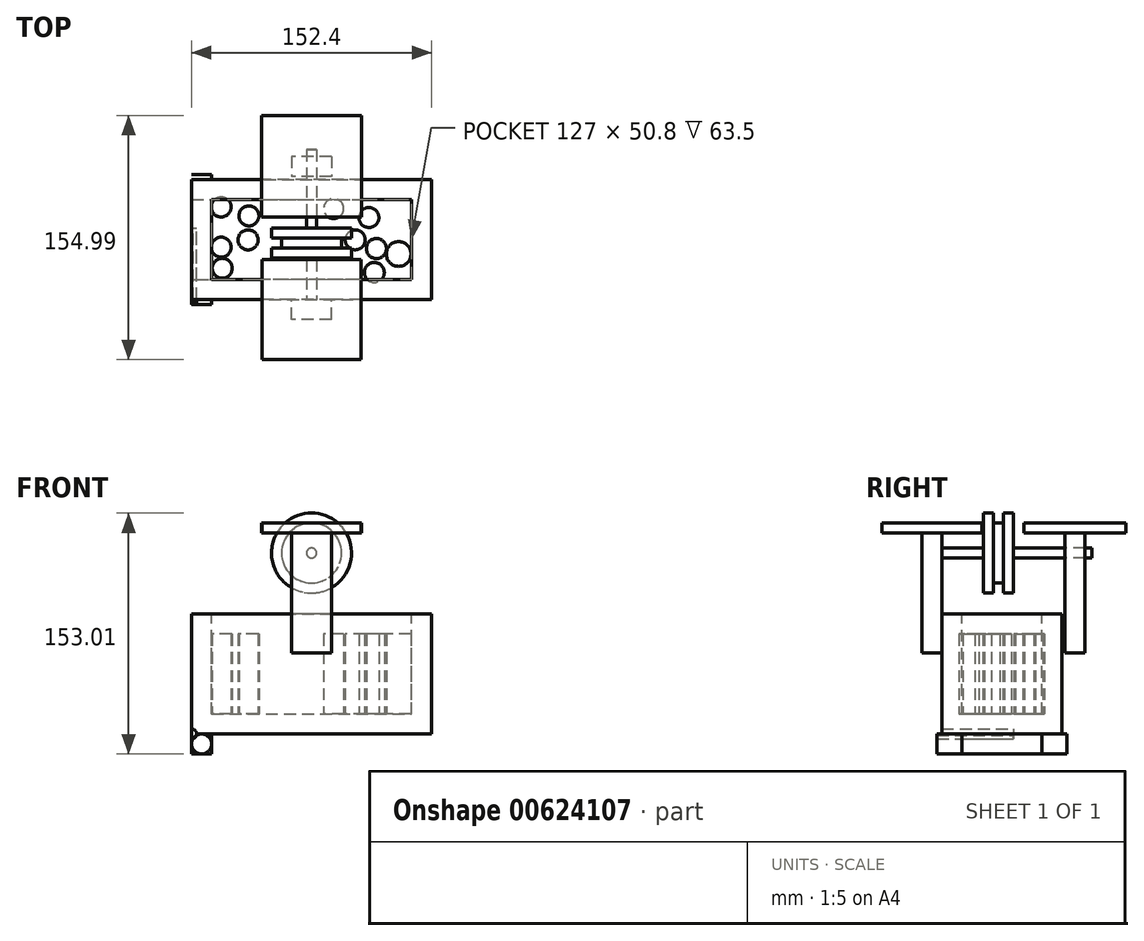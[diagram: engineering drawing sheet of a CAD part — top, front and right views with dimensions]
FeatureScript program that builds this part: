
annotation { "Feature Type Name" : "Feature", "Feature Type Description" : "" }
export const myFeature = defineFeature(function(context is Context, id is Id, definition is map)
    precondition{}
    {
        {
            var Q0;
            Q0=qCreatedBy(makeId("Front.planeOp"),FACE);
            var sketch = newSketch(context, id + "F0", { "sketchPlane" : qUnion([Q0])});
            skLineSegment(sketch, "E0", {"start": v(0, 0) * mm, "end": v(152.4, 0) * mm});
            skLineSegment(sketch, "E1", {"start": v(152.4, 0) * mm, "end": v(152.4, 76.2) * mm});
            skLineSegment(sketch, "E2", {"start": v(152.4, 76.2) * mm, "end": v(0, 76.2) * mm});
            skLineSegment(sketch, "E3", {"start": v(0, 76.2) * mm, "end": v(0, 0) * mm});
            skSolve(sketch);
        }
        {
            var Q0;
            Q0=makeQuery(id+"F0.imprint","IMPRINT",FACE,{"disambiguationData":[TD([[makeQuery(id+"F0.imprint","IMPRINT",EDGE,{"derivedFrom":sQuery(id+"F0.wireOp",EDGE,"E0")}),1.0]])]});
            extrude(context, id + "F1", {"entities" : qUnion([Q0]), "oppositeDirection" : true, "depth" : 76.2 * mm, "offsetDistance" : 25.4 * mm});
        }
        {
            var Q0;
            Q0=makeQuery(id+"F1.opExtrude","SWEPT_FACE",FACE,{"disambiguationData":[OSD([sQuery(id+"F0.wireOp",EDGE,"E2")])]});
            var sketch = newSketch(context, id + "F2", { "sketchPlane" : qUnion([Q0])});
            skLineSegment(sketch, "E4", {"start": v(12.7, 63.5) * mm, "end": v(12.7, 12.7) * mm});
            skLineSegment(sketch, "E5", {"start": v(12.7, 63.5) * mm, "end": v(139.7, 63.5) * mm});
            skLineSegment(sketch, "E6", {"start": v(139.7, 12.7) * mm, "end": v(139.7, 63.5) * mm});
            skLineSegment(sketch, "E7", {"start": v(139.7, 12.7) * mm, "end": v(12.7, 12.7) * mm});
            skSolve(sketch);
        }
        {
            var Q0;
            Q0=makeQuery(id+"F2.imprint","IMPRINT",FACE,{"disambiguationData":[TD([[makeQuery(id+"F2.imprint","IMPRINT",EDGE,{"derivedFrom":sQuery(id+"F2.wireOp",EDGE,"E4")}),1.0]])]});
            extrude(context, id + "F3", {"entities" : qUnion([Q0]), "operationType" : NewBodyOperationType.REMOVE, "oppositeDirection" : true, "depth" : 63.5 * mm, "offsetDistance" : 25.4 * mm});
        }
        {
            var Q0;
            Q0=makeQuery(id+"F1.opExtrude","CAP_FACE",FACE,{"disambiguationData":[OSD([sQuery(id+"F0.wireOp",EDGE,"E0"),sQuery(id+"F0.wireOp",EDGE,"E1"),sQuery(id+"F0.wireOp",EDGE,"E2"),sQuery(id+"F0.wireOp",EDGE,"E3")])],"isStart":true});
            var sketch = newSketch(context, id + "F4", { "sketchPlane" : qUnion([Q0])});
            skLineSegment(sketch, "E8", {"start": v(76.2, 0) * mm, "end": v(76.2, 51.42) * mm});
            skLineSegment(sketch, "E9", {"start": v(76.2, 51.42) * mm, "end": v(88.9, 51.42) * mm});
            skLineSegment(sketch, "E10", {"start": v(76.2, 51.42) * mm, "end": v(63.5, 51.42) * mm});
            skLineSegment(sketch, "E11", {"start": v(63.5, 51.42) * mm, "end": v(63.5, 64.12) * mm});
            skLineSegment(sketch, "E12", {"start": v(88.9, 51.42) * mm, "end": v(88.9, 64.12) * mm});
            skLineSegment(sketch, "E13", {"start": v(63.5, 64.12) * mm, "end": v(88.9, 64.12) * mm});
            skSolve(sketch);
        }
        {
            var Q0;
            Q0 = qSketchRegion(id + "F4", true);
            extrude(context, id + "F5", {"entities" : qUnion([Q0]), "depth" : 12.7 * mm, "offsetDistance" : 25.4 * mm});
        }
        {
            var Q0;
            Q0=makeQuery(id+"F5.opExtrude","SWEPT_FACE",FACE,{"disambiguationData":[OSD([sQuery(id+"F4.wireOp",EDGE,"E13")])]});
            var sketch = newSketch(context, id + "F6", { "sketchPlane" : qUnion([Q0])});
            skLineSegment(sketch, "E14", {"start": v(63.5, -12.7) * mm, "end": v(63.5, 0) * mm});
            skLineSegment(sketch, "E15", {"start": v(63.5, 0) * mm, "end": v(88.9, 0) * mm});
            skLineSegment(sketch, "E16", {"start": v(88.9, 0) * mm, "end": v(88.9, -12.7) * mm});
            skLineSegment(sketch, "E17", {"start": v(88.9, -12.7) * mm, "end": v(63.5, -12.7) * mm});
            skSolve(sketch);
        }
        {
            var Q0;
            Q0 = qSketchRegion(id + "F6", true);
            extrude(context, id + "F7", {"entities" : qUnion([Q0]), "depth" : 63.5 * mm, "offsetDistance" : 25.4 * mm});
        }
        {
            var Q0;
            Q0=qCreatedBy(makeId("Front.planeOp"),FACE);
            cPlane(context, id + "F8", {"entities" : qUnion([Q0]), "cplaneType" : CPlaneType.OFFSET, "offset" : 39.12 * mm, "oppositeDirection" : true, "width" : 152.4 * mm, "height" : 152.4 * mm});
        }
        {
            var Q0;
            Q0=makeQuery(id+"F5.opExtrude","SWEPT_BODY",BODY,{"disambiguationData":[OSD([sQuery(id+"F4.wireOp",EDGE,"E9"),sQuery(id+"F4.wireOp",EDGE,"E10"),sQuery(id+"F4.wireOp",EDGE,"E11"),sQuery(id+"F4.wireOp",EDGE,"E12"),sQuery(id+"F4.wireOp",EDGE,"E13")])]});
            var Q1;
            Q1=makeQuery(id+"F7.opExtrude","SWEPT_BODY",BODY,{"disambiguationData":[OSD([sQuery(id+"F6.wireOp",EDGE,"E14"),sQuery(id+"F6.wireOp",EDGE,"E15"),sQuery(id+"F6.wireOp",EDGE,"E16"),sQuery(id+"F6.wireOp",EDGE,"E17")])]});
            var Q2;
            Q2=qCreatedBy(id+"F8.planeOp",FACE);
            mirror(context, id + "F9", {"operationType" : NewBodyOperationType.ADD, "entities" : qUnion([Q0, Q1]), "mirrorPlane" : qUnion([Q2])});
        }
        {
            var Q0;
            Q0=makeQuery(id+"F9.boolean.opBoolean","MERGE",FACE,{"derivedFrom":[makeQuery(id+"F5.opExtrude","CAP_FACE",FACE,{"disambiguationData":[OSD([sQuery(id+"F4.wireOp",EDGE,"E9"),sQuery(id+"F4.wireOp",EDGE,"E10"),sQuery(id+"F4.wireOp",EDGE,"E11"),sQuery(id+"F4.wireOp",EDGE,"E12"),sQuery(id+"F4.wireOp",EDGE,"E13")])],"isStart":true}),makeQuery(id+"F7.opExtrude","SWEPT_FACE",FACE,{"disambiguationData":[OSD([sQuery(id+"F6.wireOp",EDGE,"E15")])]})]});
            var sketch = newSketch(context, id + "F10", { "sketchPlane" : qUnion([Q0])});
            skLineSegment(sketch, "E18", {"start": v(-76.2, 127.62) * mm, "end": v(-76.2, 114.92) * mm});
            skCircle(sketch, "E19", {"center": v(-76.2, 114.92) * mm, "radius": 3.18 * mm});
            skSolve(sketch);
        }
        {
            var Q0;
            Q0 = qSketchRegion(id + "F10", true);
            extrude(context, id + "F11", {"entities" : qUnion([Q0]), "depth" : 95.25 * mm, "offsetDistance" : 25.4 * mm});
        }
        {
            var Q0;
            Q0=makeQuery(id+"F7.opExtrude","CAP_FACE",FACE,{"disambiguationData":[OSD([sQuery(id+"F6.wireOp",EDGE,"E14"),sQuery(id+"F6.wireOp",EDGE,"E15"),sQuery(id+"F6.wireOp",EDGE,"E16"),sQuery(id+"F6.wireOp",EDGE,"E17")])],"isStart":false});
            var sketch = newSketch(context, id + "F12", { "sketchPlane" : qUnion([Q0])});
            skLineSegment(sketch, "E20.bottom", {"start": v(107.68, 25.4) * mm, "end": v(44.72, 25.4) * mm});
            skLineSegment(sketch, "E20.top", {"start": v(107.68, -38.1) * mm, "end": v(44.72, -38.1) * mm});
            skLineSegment(sketch, "E20.left", {"start": v(107.68, 25.4) * mm, "end": v(107.68, -38.1) * mm});
            skLineSegment(sketch, "E20.right", {"start": v(44.72, 25.4) * mm, "end": v(44.72, -38.1) * mm});
            skPoint(sketch, "E20.middle", {"position": v(76.2, -6.35) * mm});
            skPoint(sketch, "E20.middle.positionSnap0", {"position": v(76.2, -12.7) * mm});
            skPoint(sketch, "E20.middle.positionSnap1", {"position": v(88.9, -6.35) * mm});
            skPoint(sketch, "E20.centerSnap0", {"position": v(76.2, -12.7) * mm});
            skPoint(sketch, "E20.centerSnap1", {"position": v(88.9, -6.35) * mm});
            skSolve(sketch);
        }
        {
            var Q0;
            Q0 = qSketchRegion(id + "F12", true);
            extrude(context, id + "F13", {"entities" : qUnion([Q0]), "depth" : 6.35 * mm, "offsetDistance" : 25.4 * mm});
        }
        {
            var Q0;
            Q0=makeQuery(id+"F9.opPattern","COPY",FACE,{"derivedFrom":makeQuery(id+"F7.opExtrude","CAP_FACE",FACE,{"disambiguationData":[OSD([sQuery(id+"F6.wireOp",EDGE,"E14"),sQuery(id+"F6.wireOp",EDGE,"E15"),sQuery(id+"F6.wireOp",EDGE,"E16"),sQuery(id+"F6.wireOp",EDGE,"E17")])],"isStart":false}),"instanceName":"1"});
            var sketch = newSketch(context, id + "F14", { "sketchPlane" : qUnion([Q0])});
            skLineSegment(sketch, "E21.bottom", {"start": v(107.95, 52.28) * mm, "end": v(44.45, 52.28) * mm});
            skLineSegment(sketch, "E21.top", {"start": v(107.95, 116.89) * mm, "end": v(44.45, 116.89) * mm});
            skLineSegment(sketch, "E21.left", {"start": v(107.95, 52.28) * mm, "end": v(107.95, 116.89) * mm});
            skLineSegment(sketch, "E21.right", {"start": v(44.45, 52.28) * mm, "end": v(44.45, 116.89) * mm});
            skPoint(sketch, "E21.middle", {"position": v(76.2, 84.58) * mm});
            skPoint(sketch, "E21.middle.positionSnap0", {"position": v(63.5, 84.58) * mm});
            skPoint(sketch, "E21.middle.positionSnap1", {"position": v(76.2, 90.93) * mm});
            skPoint(sketch, "E21.centerSnap0", {"position": v(63.5, 84.58) * mm});
            skPoint(sketch, "E21.centerSnap1", {"position": v(76.2, 90.93) * mm});
            skSolve(sketch);
        }
        {
            var Q0;
            Q0 = qSketchRegion(id + "F14", true);
            extrude(context, id + "F15", {"entities" : qUnion([Q0]), "depth" : 6.35 * mm, "offsetDistance" : 25.4 * mm});
        }
        {
            var Q0;
            Q0=makeQuery(id+"F1.opExtrude","SWEPT_FACE",FACE,{"disambiguationData":[OSD([sQuery(id+"F0.wireOp",EDGE,"E0")])]});
            var sketch = newSketch(context, id + "F16", { "sketchPlane" : qUnion([Q0])});
            skLineSegment(sketch, "E22", {"start": v(0, -12.7) * mm, "end": v(12.7, -12.7) * mm});
            skLineSegment(sketch, "E23", {"start": v(0, -63.5) * mm, "end": v(12.7, -63.5) * mm});
            skLineSegment(sketch, "E24", {"start": v(12.7, -12.7) * mm, "end": v(12.7, -63.5) * mm});
            skSolve(sketch);
        }
        {
            var Q0;
            {var subQ0=sQuery(id+"F16.wireOp",EDGE,"E22");Q0=makeQuery(id+"F16.imprint","IMPRINT",FACE,{"disambiguationData":[TD([[makeQuery(id+"F16.imprint","IMPRINT",EDGE,{"derivedFrom":subQ0}),-1.0]])]});}
            extrude(context, id + "F17", {"entities" : qUnion([Q0]), "operationType" : NewBodyOperationType.ADD, "depth" : 12.7 * mm, "offsetDistance" : 25.4 * mm});
        }
        {
            var Q0;
            Q0=makeQuery(id+"F17.opExtrude","SWEPT_FACE",FACE,{"disambiguationData":[OSD([sQuery(id+"F16.wireOp",EDGE,"E22")])]});
            var sketch = newSketch(context, id + "F18", { "sketchPlane" : qUnion([Q0])});
            skCircle(sketch, "E25", {"center": v(6.35, -6.35) * mm, "radius": 6.35 * mm});
            skPoint(sketch, "E25.centerSnap0", {"position": v(6.35, -12.7) * mm});
            skPoint(sketch, "E25.centerSnap1", {"position": v(0, -6.35) * mm});
            skSolve(sketch);
        }
        {
            var Q0;
            Q0 = qSketchRegion(id + "F18", true);
            extrude(context, id + "F19", {"entities" : qUnion([Q0]), "endBound" : BoundingType.SYMMETRIC, "oppositeDirection" : true, "depth" : 133.6 * mm, "offsetDistance" : 25.4 * mm});
        }
        {
            var Q0;
            Q0=makeQuery(id+"F19.opExtrude","CAP_FACE",FACE,{"disambiguationData":[OSD([sQuery(id+"F18.wireOp",EDGE,"E25")])],"isStart":true});
            extrude(context, id + "F20", {"entities" : qUnion([Q0]), "operationType" : NewBodyOperationType.REMOVE, "oppositeDirection" : true, "depth" : 51.05 * mm, "offsetDistance" : 25.4 * mm});
        }
        {
            var Q0;
            Q0=qCreatedBy(id+"F8.planeOp",FACE);
            var sketch = newSketch(context, id + "F21", { "sketchPlane" : qUnion([Q0])});
            skCircle(sketch, "E26", {"center": v(76.17, 114.9) * mm, "radius": 19.05 * mm});
            skSolve(sketch);
        }
        {
            var Q0;
            Q0=makeQuery(id+"F21.imprint","IMPRINT",FACE,{"disambiguationData":[TD([[makeQuery(id+"F21.imprint","IMPRINT",EDGE,{"derivedFrom":sQuery(id+"F21.wireOp",EDGE,"E26")}),1.0]])]});
            extrude(context, id + "F22", {"entities" : qUnion([Q0]), "depth" : 6.35 * mm, "offsetDistance" : 25.4 * mm});
        }
        {
            var Q0;
            Q0=makeQuery(id+"F22.opExtrude","CAP_FACE",FACE,{"disambiguationData":[OSD([sQuery(id+"F21.wireOp",EDGE,"E26")])],"isStart":false});
            var sketch = newSketch(context, id + "F23", { "sketchPlane" : qUnion([Q0])});
            skCircle(sketch, "E27", {"center": v(76.17, 114.9) * mm, "radius": 25.4 * mm});
            skSolve(sketch);
        }
        {
            var Q0;
            Q0 = qSketchRegion(id + "F23", true);
            extrude(context, id + "F24", {"entities" : qUnion([Q0]), "operationType" : NewBodyOperationType.ADD, "depth" : 6.35 * mm, "offsetDistance" : 25.4 * mm});
        }
        {
            var Q0;
            Q0=makeQuery(id+"F22.opExtrude","CAP_FACE",FACE,{"disambiguationData":[OSD([sQuery(id+"F21.wireOp",EDGE,"E26")])],"isStart":true});
            var sketch = newSketch(context, id + "F25", { "sketchPlane" : qUnion([Q0])});
            skCircle(sketch, "E28", {"center": v(-76.17, 114.9) * mm, "radius": 25.4 * mm});
            skSolve(sketch);
        }
        {
            var Q0;
            Q0 = qSketchRegion(id + "F25", true);
            extrude(context, id + "F26", {"entities" : qUnion([Q0]), "operationType" : NewBodyOperationType.ADD, "depth" : 6.35 * mm, "offsetDistance" : 25.4 * mm});
        }
        {
            var Q0;
            Q0=makeQuery(id+"F26.opExtrude","CAP_FACE",FACE,{"disambiguationData":[OSD([sQuery(id+"F25.wireOp",EDGE,"E28")])],"isStart":false});
            var sketch = newSketch(context, id + "F27", { "sketchPlane" : qUnion([Q0])});
            skCircle(sketch, "E29", {"center": v(0, 0) * mm, "radius": 3.17 * mm});
            skSolve(sketch);
        }
        {
            var Q0;
            Q0 = qSketchRegion(id + "F27", true);
            extrude(context, id + "F28", {"entities" : qUnion([Q0]), "operationType" : NewBodyOperationType.REMOVE, "oppositeDirection" : true, "depth" : 95.5 * mm, "offsetDistance" : 25.4 * mm});
        }
        {
            var Q0;
            Q0=makeQuery(id+"F3.boolean.opBoolean","COPY",FACE,{"derivedFrom":makeQuery(id+"F3.opExtrude","CAP_FACE",FACE,{"disambiguationData":[OSD([sQuery(id+"F2.wireOp",EDGE,"E4"),sQuery(id+"F2.wireOp",EDGE,"E5"),sQuery(id+"F2.wireOp",EDGE,"E6"),sQuery(id+"F2.wireOp",EDGE,"E7")])],"isStart":false})});
            var sketch = newSketch(context, id + "F29", { "sketchPlane" : qUnion([Q0])});
            skSolve(sketch);
        }
        {
            var Q0;
            Q0=makeQuery(id+"F29.imprint","IMPRINT",FACE,{"disambiguationData":[TD([[makeQuery(id+"F29.imprint","IMPRINT",EDGE,{"derivedFrom":makeQuery(id+"F3.boolean.opBoolean","COPY",EDGE,{"derivedFrom":makeQuery(id+"F3.opExtrude","CAP_EDGE",EDGE,{"disambiguationData":[OSD([sQuery(id+"F2.wireOp",EDGE,"E4")])],"isStart":false})})}),1.0]])]});
            var sketch = newSketch(context, id + "F30", { "sketchPlane" : qUnion([Q0])});
            skCircle(sketch, "E30", {"center": v(36.43, 53.17) * mm, "radius": 6.35 * mm});
            skCircle(sketch, "E31", {"center": v(35.9, 37.93) * mm, "radius": 6.35 * mm});
            skCircle(sketch, "E32", {"center": v(112.63, 52.12) * mm, "radius": 6.35 * mm});
            skCircle(sketch, "E33", {"center": v(103.96, 37.93) * mm, "radius": 6.35 * mm});
            skCircle(sketch, "E34", {"center": v(117.36, 32.42) * mm, "radius": 6.35 * mm});
            skCircle(sketch, "E35", {"center": v(18.82, 58.78) * mm, "radius": 6.35 * mm});
            skCircle(sketch, "E36", {"center": v(18.82, 33.3) * mm, "radius": 6.35 * mm});
            skCircle(sketch, "E37", {"center": v(116.07, 17.2) * mm, "radius": 6.35 * mm});
            skCircle(sketch, "E38", {"center": v(131.5, 28.94) * mm, "radius": 7.83 * mm});
            skCircle(sketch, "E39", {"center": v(90.25, 57.78) * mm, "radius": 6.35 * mm});
            skCircle(sketch, "E40", {"center": v(19.49, 19.88) * mm, "radius": 6.35 * mm});
            skSolve(sketch);
        }
        {
            var Q0;
            Q0 = qSketchRegion(id + "F30", true);
            extrude(context, id + "F31", {"entities" : qUnion([Q0]), "depth" : 50.8 * mm, "offsetDistance" : 25.4 * mm});
        }
    });
